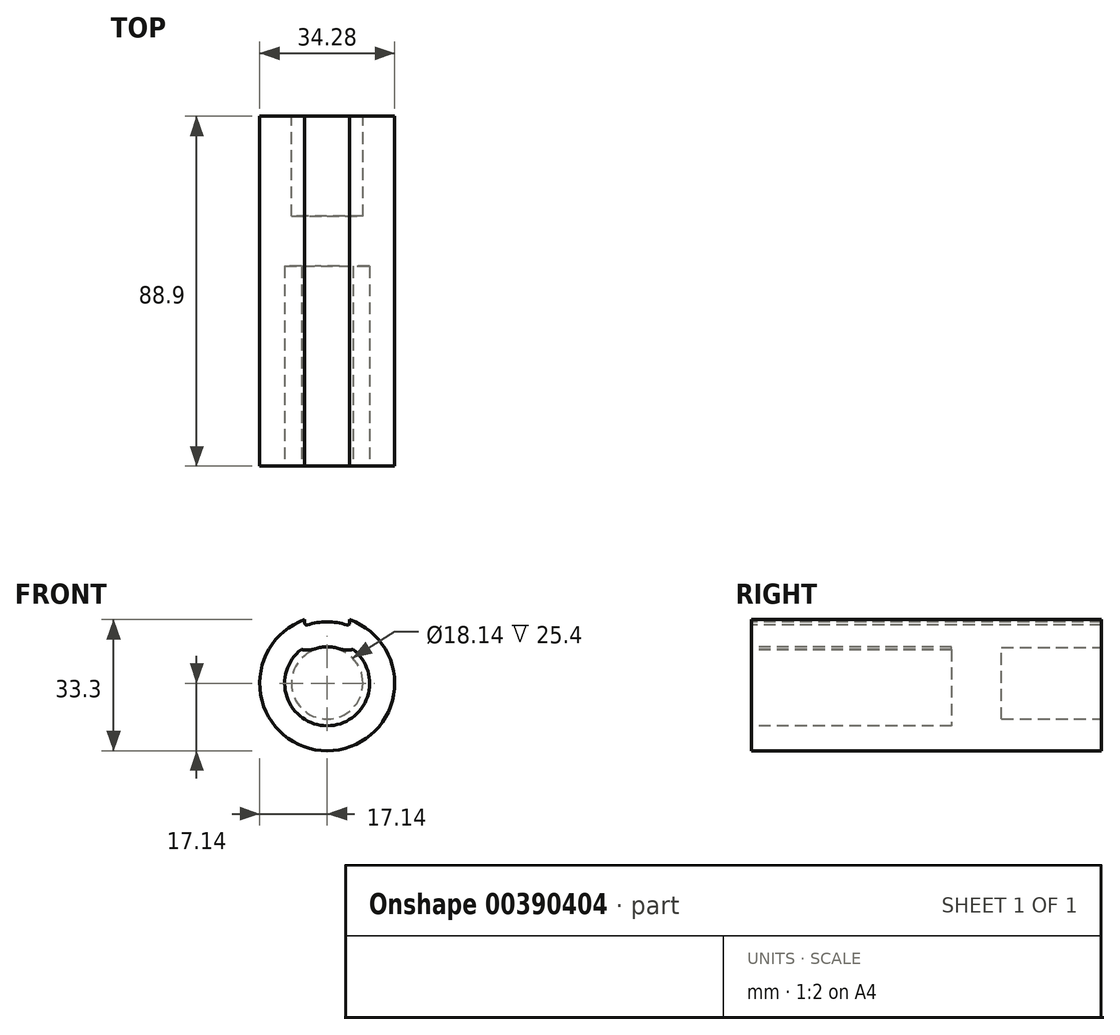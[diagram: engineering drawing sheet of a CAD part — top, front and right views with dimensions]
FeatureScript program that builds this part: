
annotation { "Feature Type Name" : "Feature", "Feature Type Description" : "" }
export const myFeature = defineFeature(function(context is Context, id is Id, definition is map)
    precondition{}
    {
        {
            var Q0;
            Q0=qCreatedBy(makeId("Front.planeOp"),FACE);
            var sketch = newSketch(context, id + "F0", { "sketchPlane" : qUnion([Q0])});
            skCircle(sketch, "E0", {"center": v(0, 0) * mm, "radius": 17.15 * mm});
            skCircle(sketch, "E1", {"center": v(0, 0) * mm, "radius": 9.07 * mm});
            skSolve(sketch);
        }
        {
            var Q0;
            Q0=makeQuery(id+"F0.imprint","IMPRINT",FACE,{"disambiguationData":[TD([[makeQuery(id+"F0.imprint","IMPRINT",EDGE,{"derivedFrom":sQuery(id+"F0.wireOp",EDGE,"E1")}),1.0]])]});
            var Q1;
            Q1=makeQuery(id+"F0.imprint","IMPRINT",FACE,{"disambiguationData":[TD([[makeQuery(id+"F0.imprint","IMPRINT",EDGE,{"derivedFrom":sQuery(id+"F0.wireOp",EDGE,"E0")}),1.0]])]});
            extrude(context, id + "F1", {"entities" : qUnion([Q0, Q1]), "depth" : 88.9 * mm});
        }
        {
            var Q0;
            Q0=makeQuery(id+"F0.imprint","IMPRINT",FACE,{"disambiguationData":[TD([[makeQuery(id+"F0.imprint","IMPRINT",EDGE,{"derivedFrom":sQuery(id+"F0.wireOp",EDGE,"E1")}),1.0]])]});
            extrude(context, id + "F2", {"entities" : qUnion([Q0]), "operationType" : NewBodyOperationType.REMOVE, "depth" : 25.4 * mm});
        }
        {
            var Q0;
            Q0=makeQuery(id+"F1.opExtrude","CAP_FACE",FACE,{"disambiguationData":[OSD([sQuery(id+"F0.wireOp",EDGE,"E0")])],"isStart":false});
            var sketch = newSketch(context, id + "F3", { "sketchPlane" : qUnion([Q0])});
            skCircle(sketch, "E2", {"center": v(0, -0.76) * mm, "radius": 16.38 * mm});
            skLineSegment(sketch, "E3.bottom", {"start": v(5.71, 17.15) * mm, "end": v(-5.72, 17.15) * mm});
            skLineSegment(sketch, "E3.top", {"start": v(5.71, 14.6) * mm, "end": v(-5.72, 14.6) * mm});
            skLineSegment(sketch, "E3.left", {"start": v(5.71, 17.15) * mm, "end": v(5.71, 14.6) * mm});
            skLineSegment(sketch, "E3.right", {"start": v(-5.72, 17.15) * mm, "end": v(-5.72, 14.6) * mm});
            skPoint(sketch, "E3.middle", {"position": v(0, 15.87) * mm});
            skSolve(sketch);
        }
        {
            var Q0;
            {var subQ4=makeQuery(id+"F1.opExtrude","CAP_EDGE",EDGE,{"disambiguationData":[OSD([sQuery(id+"F0.wireOp",EDGE,"E0")])],"isStart":false});var subQ6=makeQuery(id+"F3.imprint","INTERSECT",VERTEX,{"derivedFrom":[subQ4,sQuery(id+"F3.wireOp",EDGE,"E3.bottom")]});Q0=makeQuery(id+"F3.imprint","IMPRINT",FACE,{"disambiguationData":[TD([[makeQuery(id+"F3.imprint","IMPRINT",EDGE,{"disambiguationData":[TD([[subQ6,1.0]])],"derivedFrom":subQ4}),1.0]])]});}
            extrude(context, id + "F4", {"entities" : qUnion([Q0]), "operationType" : NewBodyOperationType.REMOVE, "endBound" : BoundingType.THROUGH_ALL, "oppositeDirection" : true, "depth" : 25.4 * mm});
        }
        {
            var Q0;
            Q0=makeQuery(id+"F4.boolean.opBoolean","COPY",EDGE,{"derivedFrom":makeQuery(id+"F4.opExtrude","SWEPT_EDGE",EDGE,{"disambiguationData":[OSD([sQuery(id+"F0.wireOp",EDGE,"E0"),sQuery(id+"F3.wireOp",EDGE,"E3.right")])]})});
            var Q1;
            Q1=makeQuery(id+"F4.boolean.opBoolean","COPY",EDGE,{"derivedFrom":makeQuery(id+"F4.opExtrude","SWEPT_EDGE",EDGE,{"disambiguationData":[OSD([sQuery(id+"F0.wireOp",EDGE,"E0"),sQuery(id+"F3.wireOp",EDGE,"E3.left")])]})});
            var Q2;
            Q2=makeQuery(id+"F4.boolean.opBoolean","COPY",EDGE,{"derivedFrom":makeQuery(id+"F4.opExtrude","SWEPT_EDGE",EDGE,{"disambiguationData":[OSD([sQuery(id+"F3.wireOp",EDGE,"E2"),sQuery(id+"F3.wireOp",EDGE,"E3.top"),sQuery(id+"F3.wireOp",EDGE,"E3.right")])]})});
            var Q3;
            Q3=makeQuery(id+"F4.boolean.opBoolean","COPY",EDGE,{"derivedFrom":makeQuery(id+"F4.opExtrude","SWEPT_EDGE",EDGE,{"disambiguationData":[OSD([sQuery(id+"F3.wireOp",EDGE,"E2"),sQuery(id+"F3.wireOp",EDGE,"E3.top"),sQuery(id+"F3.wireOp",EDGE,"E3.left")])]})});
            fillet(context, id + "F5", {"entities" : qUnion([Q0, Q1, Q2, Q3]), "radius" : 0.5 * mm, "tangentPropagation" : true, "allowEdgeOverflow" : false});
        }
        {
            var Q0;
            Q0=makeQuery(id+"F1.opExtrude","CAP_FACE",FACE,{"disambiguationData":[OSD([sQuery(id+"F0.wireOp",EDGE,"E0")])],"isStart":false});
            var sketch = newSketch(context, id + "F6", { "sketchPlane" : qUnion([Q0])});
            skArc(sketch, "E4.0", {"start": v(-6.55, 8.58) * mm, "mid": v(0, -10.8) * mm, "end": v(6.55, 8.58) * mm});
            skArc(sketch, "E4.1", {"start": v(-3.1, 8.78) * mm, "mid": v(-4.8, 8.46) * mm, "end": v(-6.55, 8.58) * mm});
            skArc(sketch, "E4.2", {"start": v(3.1, 8.78) * mm, "mid": v(0, 9.27) * mm, "end": v(-3.1, 8.78) * mm});
            skArc(sketch, "E4.3", {"start": v(6.55, 8.58) * mm, "mid": v(4.8, 8.46) * mm, "end": v(3.1, 8.78) * mm});
            skSolve(sketch);
        }
        {
            var Q0;
            Q0=makeQuery(id+"F6.imprint","IMPRINT",FACE,{"disambiguationData":[TD([[makeQuery(id+"F6.imprint","IMPRINT",EDGE,{"derivedFrom":sQuery(id+"F6.wireOp",EDGE,"E4.0")}),1.0]])]});
            extrude(context, id + "F7", {"entities" : qUnion([Q0]), "operationType" : NewBodyOperationType.REMOVE, "oppositeDirection" : true, "depth" : 50.8 * mm});
        }
    });
